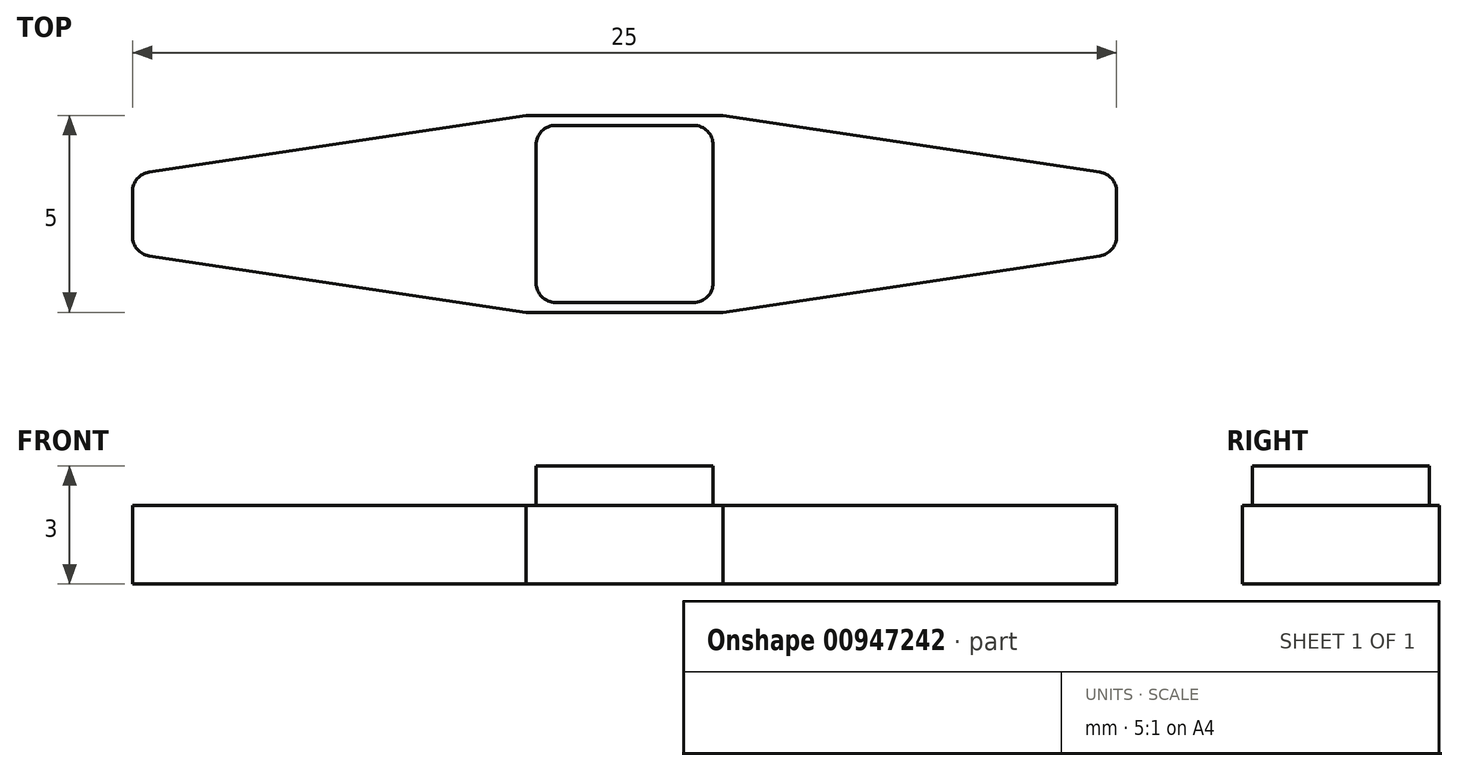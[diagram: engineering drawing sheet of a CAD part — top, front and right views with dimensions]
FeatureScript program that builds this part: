
annotation { "Feature Type Name" : "Feature", "Feature Type Description" : "" }
export const myFeature = defineFeature(function(context is Context, id is Id, definition is map)
    precondition{}
    {
        {
            var Q0;
            Q0=qCreatedBy(makeId("Top.planeOp"),FACE);
            var sketch = newSketch(context, id + "F0", { "sketchPlane" : qUnion([Q0])});
            skLineSegment(sketch, "E0.bottom", {"start": v(-1.75, 2.25) * mm, "end": v(1.75, 2.25) * mm});
            skLineSegment(sketch, "E0.top", {"start": v(-1.75, -2.25) * mm, "end": v(1.75, -2.25) * mm});
            skLineSegment(sketch, "E0.left", {"start": v(-2.25, 1.75) * mm, "end": v(-2.25, -1.75) * mm});
            skLineSegment(sketch, "E0.right", {"start": v(2.25, 1.75) * mm, "end": v(2.25, -1.75) * mm});
            skPoint(sketch, "E1", {"position": v(-2.25, 0) * mm});
            skPoint(sketch, "E2", {"position": v(0, 2.25) * mm});
            skPoint(sketch, "E3.visualSharp", {"position": v(-2.25, 2.25) * mm});
            skArc(sketch, "E3.filletArc", {"start": v(-1.75, 2.25) * mm, "mid": v(-2.1, 2.1) * mm, "end": v(-2.25, 1.75) * mm});
            skPoint(sketch, "E4.visualSharp", {"position": v(-2.25, -2.25) * mm});
            skArc(sketch, "E4.filletArc", {"start": v(-2.25, -1.75) * mm, "mid": v(-2.1, -2.1) * mm, "end": v(-1.75, -2.25) * mm});
            skPoint(sketch, "E5.visualSharp", {"position": v(2.25, -2.25) * mm});
            skArc(sketch, "E5.filletArc", {"start": v(1.75, -2.25) * mm, "mid": v(2.1, -2.1) * mm, "end": v(2.25, -1.75) * mm});
            skPoint(sketch, "E6.visualSharp", {"position": v(2.25, 2.25) * mm});
            skArc(sketch, "E6.filletArc", {"start": v(2.25, 1.75) * mm, "mid": v(2.1, 2.1) * mm, "end": v(1.75, 2.25) * mm});
            skSolve(sketch);
        }
        {
            var Q0;
            Q0 = qSketchRegion(id + "F0", true);
            extrude(context, id + "F1", {"entities" : qUnion([Q0]), "depth" : 1 * mm, "offsetDistance" : 25 * mm});
        }
        {
            var Q0;
            Q0=qCreatedBy(makeId("Top.planeOp"),FACE);
            var sketch = newSketch(context, id + "F2", { "sketchPlane" : qUnion([Q0])});
            skLineSegment(sketch, "E7.bottom", {"start": v(-2.5, -2.5) * mm, "end": v(2.5, -2.5) * mm});
            skLineSegment(sketch, "E7.top", {"start": v(-2.5, 2.5) * mm, "end": v(2.5, 2.5) * mm});
            skLineSegment(sketch, "E7.left", {"start": v(-2.5, -2.5) * mm, "end": v(-2.5, 2.5) * mm});
            skLineSegment(sketch, "E7.right", {"start": v(2.5, -2.5) * mm, "end": v(2.5, 2.5) * mm});
            skPoint(sketch, "E8", {"position": v(0, -2.5) * mm});
            skPoint(sketch, "E9", {"position": v(-2.5, 0) * mm});
            skLineSegment(sketch, "E10", {"start": v(-2.5, -2.5) * mm, "end": v(-12.07, -1.06) * mm});
            skLineSegment(sketch, "E11", {"start": v(-12.5, -0.57) * mm, "end": v(-12.5, 0.57) * mm});
            skLineSegment(sketch, "E12", {"start": v(-12.07, 1.06) * mm, "end": v(-2.5, 2.5) * mm});
            skPoint(sketch, "E13", {"position": v(-12.5, 0) * mm});
            skPoint(sketch, "E14.visualSharp", {"position": v(-12.5, -1) * mm});
            skArc(sketch, "E14.filletArc", {"start": v(-12.5, -0.57) * mm, "mid": v(-12.38, -0.9) * mm, "end": v(-12.07, -1.06) * mm});
            skPoint(sketch, "E15.visualSharp", {"position": v(-12.5, 1) * mm});
            skArc(sketch, "E15.filletArc", {"start": v(-12.07, 1.06) * mm, "mid": v(-12.38, 0.9) * mm, "end": v(-12.5, 0.57) * mm});
            skPoint(sketch, "E16.visualSharp", {"position": v(-2.5, -2.5) * mm});
            skPoint(sketch, "E17.visualSharp", {"position": v(-2.5, 2.5) * mm});
            skLineSegment(sketch, "E18.MirrorCS", {"start": v(2.5, -2.5) * mm, "end": v(12.07, -1.06) * mm});
            skArc(sketch, "E19.MirrorCS", {"start": v(12.5, -0.57) * mm, "mid": v(12.38, -0.9) * mm, "end": v(12.07, -1.06) * mm});
            skLineSegment(sketch, "E20.MirrorCS", {"start": v(12.5, -0.57) * mm, "end": v(12.5, 0.57) * mm});
            skArc(sketch, "E21.MirrorCS", {"start": v(12.07, 1.06) * mm, "mid": v(12.38, 0.9) * mm, "end": v(12.5, 0.57) * mm});
            skLineSegment(sketch, "E22.MirrorCS", {"start": v(12.07, 1.06) * mm, "end": v(2.5, 2.5) * mm});
            skSolve(sketch);
        }
        {
            var Q0;
            Q0 = qSketchRegion(id + "F2", true);
            extrude(context, id + "F3", {"entities" : qUnion([Q0]), "operationType" : NewBodyOperationType.ADD, "oppositeDirection" : true, "depth" : 2 * mm, "offsetDistance" : 25 * mm});
        }
    });
